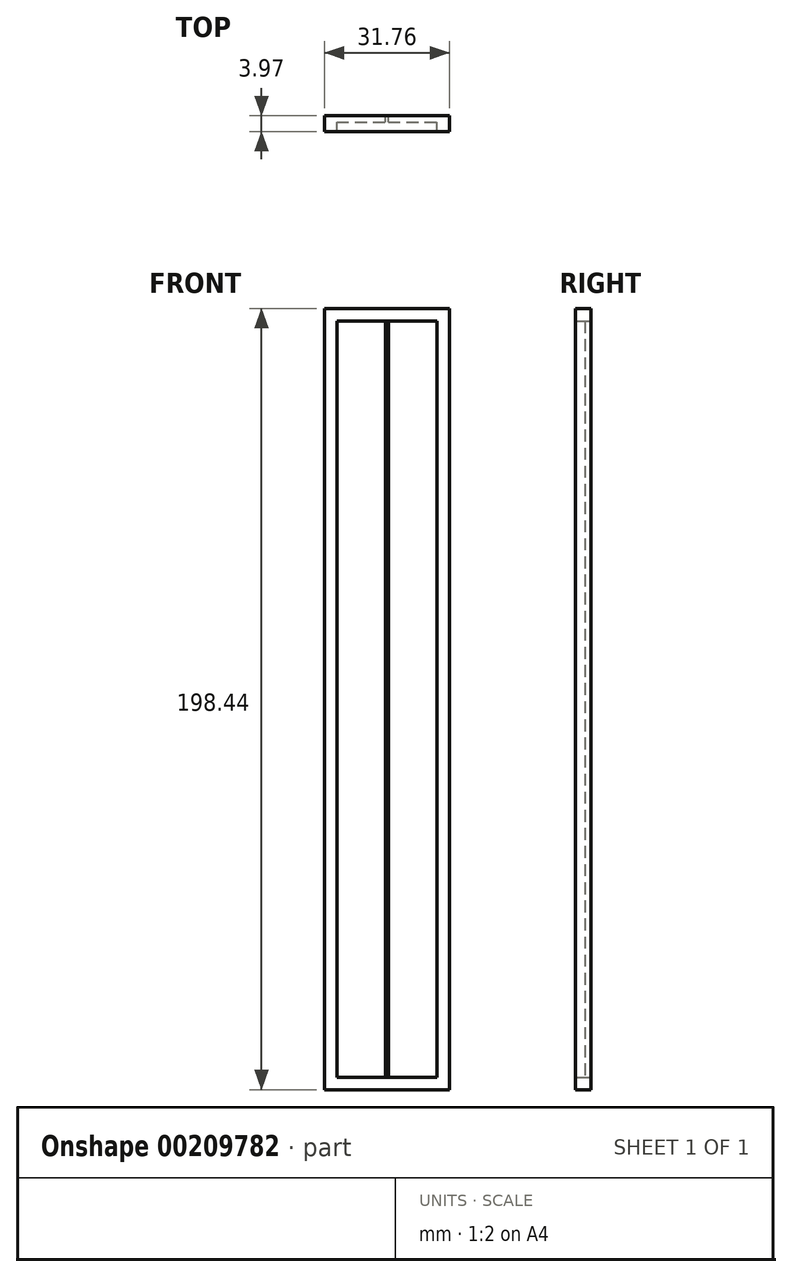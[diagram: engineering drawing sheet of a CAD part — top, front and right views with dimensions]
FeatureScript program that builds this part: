
annotation { "Feature Type Name" : "Feature", "Feature Type Description" : "" }
export const myFeature = defineFeature(function(context is Context, id is Id, definition is map)
    precondition{}
    {
        {
            var Q0;
            Q0=qCreatedBy(makeId("Front.planeOp"),FACE);
            var sketch = newSketch(context, id + "F0", { "sketchPlane" : qUnion([Q0])});
            skLineSegment(sketch, "E0.top", {"start": v(-12.7, -96.04) * mm, "end": v(12.7, -96.04) * mm});
            skLineSegment(sketch, "E0.left", {"start": v(-12.7, 96.04) * mm, "end": v(-12.7, -96.04) * mm});
            skLineSegment(sketch, "E0.right", {"start": v(12.7, 96.04) * mm, "end": v(12.7, -96.04) * mm});
            skLineSegment(sketch, "E1.top", {"start": v(-15.88, -99.22) * mm, "end": v(15.87, -99.22) * mm});
            skLineSegment(sketch, "E1.left", {"start": v(-15.88, 99.22) * mm, "end": v(-15.88, -99.22) * mm});
            skLineSegment(sketch, "E1.right", {"start": v(15.87, 99.22) * mm, "end": v(15.87, -99.22) * mm});
            skLineSegment(sketch, "E2", {"start": v(-15.88, 99.22) * mm, "end": v(15.87, 99.22) * mm});
            skLineSegment(sketch, "E3", {"start": v(-12.7, 0) * mm, "end": v(0, 0) * mm});
            skLineSegment(sketch, "E4", {"start": v(0, 0) * mm, "end": v(12.7, 0) * mm});
            skLineSegment(sketch, "E5", {"start": v(-12.7, 96.04) * mm, "end": v(-15.88, 99.22) * mm});
            skLineSegment(sketch, "E6", {"start": v(12.7, 96.04) * mm, "end": v(15.87, 99.22) * mm});
            skLineSegment(sketch, "E7", {"start": v(12.7, -96.04) * mm, "end": v(15.87, -99.22) * mm});
            skLineSegment(sketch, "E8", {"start": v(-12.7, -96.04) * mm, "end": v(-15.88, -99.22) * mm});
            skLineSegment(sketch, "E9.bottom", {"start": v(0.38, 96.04) * mm, "end": v(-0.38, 96.04) * mm});
            skLineSegment(sketch, "E9.top", {"start": v(0.38, -96.04) * mm, "end": v(-0.38, -96.04) * mm});
            skLineSegment(sketch, "E9.left", {"start": v(0.38, 96.04) * mm, "end": v(0.38, -96.04) * mm});
            skLineSegment(sketch, "E9.right", {"start": v(-0.38, 96.04) * mm, "end": v(-0.38, -96.04) * mm});
            skPoint(sketch, "E9.middle", {"position": v(0, 0) * mm});
            skLineSegment(sketch, "E10", {"start": v(-12.7, 96.04) * mm, "end": v(12.7, 96.04) * mm});
            skSolve(sketch);
        }
        {
            var Q0;
            Q0=makeQuery(id+"F0.imprint","IMPRINT",FACE,{"disambiguationData":[TD([[makeQuery(id+"F0.imprint","IMPRINT",EDGE,{"derivedFrom":sQuery(id+"F0.wireOp",EDGE,"E1.right")}),-1.0]])]});
            var Q1;
            Q1=makeQuery(id+"F0.imprint","IMPRINT",FACE,{"disambiguationData":[TD([[makeQuery(id+"F0.imprint","IMPRINT",EDGE,{"derivedFrom":sQuery(id+"F0.wireOp",EDGE,"E1.left")}),1.0]])]});
            var Q2;
            Q2=makeQuery(id+"F0.imprint","IMPRINT",FACE,{"disambiguationData":[TD([[makeQuery(id+"F0.imprint","IMPRINT",EDGE,{"derivedFrom":sQuery(id+"F0.wireOp",EDGE,"E2")}),-1.0]])]});
            var Q3;
            Q3=makeQuery(id+"F0.imprint","IMPRINT",FACE,{"disambiguationData":[TD([[makeQuery(id+"F0.imprint","IMPRINT",EDGE,{"derivedFrom":sQuery(id+"F0.wireOp",EDGE,"E1.top")}),1.0]])]});
            extrude(context, id + "F1", {"entities" : qUnion([Q0, Q1, Q2, Q3]), "depth" : 3.97 * mm});
        }
        {
            var Q0;
            {var subQ1=sQuery(id+"F0.wireOp",EDGE,"E0.right");var subQ3=sQuery(id+"F0.wireOp",EDGE,"E4");var subQ4=makeQuery(id+"F0.imprint","INTERSECT",VERTEX,{"derivedFrom":[subQ1,subQ3]});Q0=makeQuery(id+"F0.imprint","IMPRINT",FACE,{"disambiguationData":[TD([[makeQuery(id+"F0.imprint","IMPRINT",EDGE,{"disambiguationData":[TD([[subQ4,1.0]])],"derivedFrom":subQ3}),1.0]])]});}
            var Q1;
            {var subQ1=sQuery(id+"F0.wireOp",EDGE,"E0.left");var subQ3=sQuery(id+"F0.wireOp",EDGE,"E3");var subQ4=makeQuery(id+"F0.imprint","INTERSECT",VERTEX,{"derivedFrom":[subQ1,subQ3]});Q1=makeQuery(id+"F0.imprint","IMPRINT",FACE,{"disambiguationData":[TD([[makeQuery(id+"F0.imprint","IMPRINT",EDGE,{"disambiguationData":[TD([[subQ4,-1.0]])],"derivedFrom":subQ3}),1.0]])]});}
            var Q2;
            {var subQ0=sQuery(id+"F0.wireOp",EDGE,"E0.left");var subQ5=sQuery(id+"F0.wireOp",EDGE,"E3");var subQ6=makeQuery(id+"F0.imprint","INTERSECT",VERTEX,{"derivedFrom":[subQ0,subQ5]});Q2=makeQuery(id+"F0.imprint","IMPRINT",FACE,{"disambiguationData":[TD([[makeQuery(id+"F0.imprint","IMPRINT",EDGE,{"disambiguationData":[TD([[subQ6,-1.0]])],"derivedFrom":subQ5}),-1.0]])]});}
            var Q3;
            {var subQ0=sQuery(id+"F0.wireOp",EDGE,"E0.right");var subQ5=sQuery(id+"F0.wireOp",EDGE,"E4");var subQ6=makeQuery(id+"F0.imprint","INTERSECT",VERTEX,{"derivedFrom":[subQ0,subQ5]});Q3=makeQuery(id+"F0.imprint","IMPRINT",FACE,{"disambiguationData":[TD([[makeQuery(id+"F0.imprint","IMPRINT",EDGE,{"disambiguationData":[TD([[subQ6,1.0]])],"derivedFrom":subQ5}),-1.0]])]});}
            extrude(context, id + "F2", {"entities" : qUnion([Q0, Q1, Q2, Q3]), "operationType" : NewBodyOperationType.ADD, "depth" : 1.59 * mm});
        }
    });
